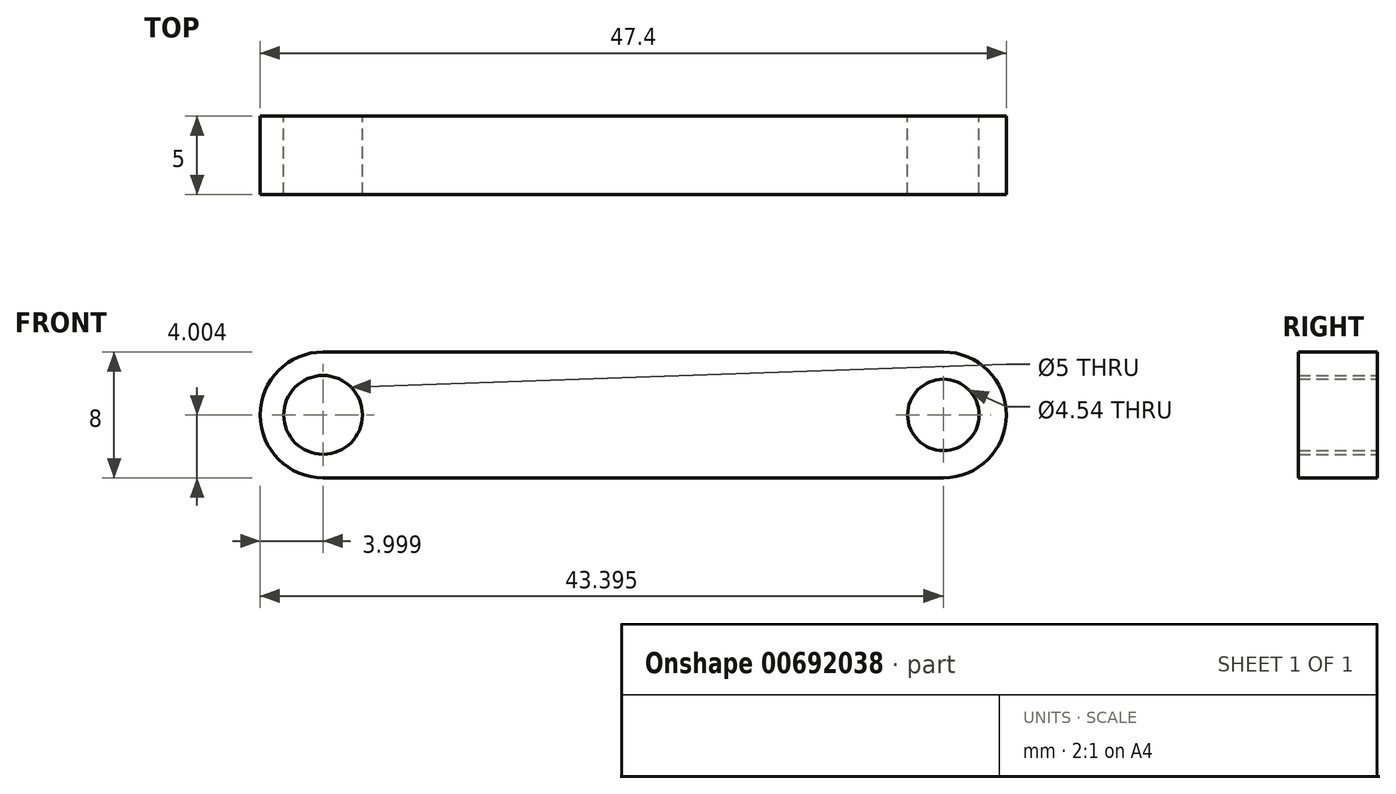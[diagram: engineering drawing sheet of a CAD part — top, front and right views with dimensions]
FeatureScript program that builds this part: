
annotation { "Feature Type Name" : "Feature", "Feature Type Description" : "" }
export const myFeature = defineFeature(function(context is Context, id is Id, definition is map)
    precondition{}
    {
        {
            var Q0;
            Q0=qCreatedBy(makeId("Front.planeOp"),FACE);
            var sketch = newSketch(context, id + "F0", { "sketchPlane" : qUnion([Q0])});
            skLineSegment(sketch, "E0.bottom", {"start": v(-27.3, 3.15) * mm, "end": v(12.1, 3.15) * mm});
            skLineSegment(sketch, "E0.top", {"start": v(-27.3, -4.85) * mm, "end": v(12.1, -4.85) * mm});
            skArc(sketch, "E1", {"start": v(-27.3, 3.15) * mm, "mid": v(-31.3, -0.85) * mm, "end": v(-27.3, -4.85) * mm});
            skArc(sketch, "E2", {"start": v(12.1, -4.85) * mm, "mid": v(16.1, -0.85) * mm, "end": v(12.1, 3.15) * mm});
            skCircle(sketch, "E3", {"center": v(-27.3, -0.85) * mm, "radius": 2.5 * mm});
            skCircle(sketch, "E4", {"center": v(12.1, -0.85) * mm, "radius": 2.27 * mm});
            skSolve(sketch);
        }
        {
            var Q0;
            Q0=makeQuery(id+"F0.imprint","IMPRINT",FACE,{"disambiguationData":[TD([[makeQuery(id+"F0.imprint","IMPRINT",EDGE,{"derivedFrom":sQuery(id+"F0.wireOp",EDGE,"E0.bottom")}),-1.0]])]});
            extrude(context, id + "F1", {"entities" : qUnion([Q0]), "depth" : 5 * mm, "offsetDistance" : 25 * mm});
        }
    });
